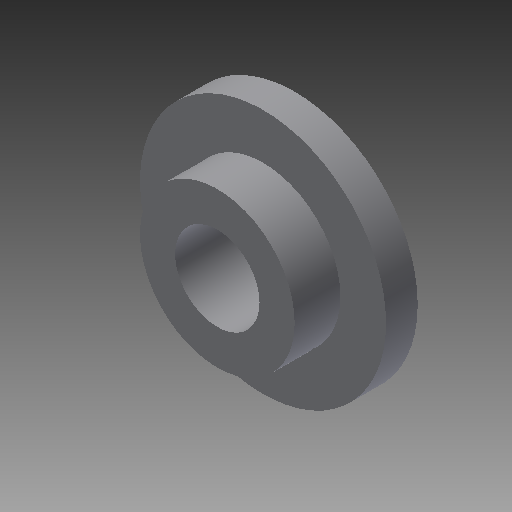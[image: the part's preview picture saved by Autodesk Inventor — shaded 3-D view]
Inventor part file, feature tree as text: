
AUTODESK INVENTOR PART (.ipt)
format: ipt  version: 2017 SP1 (Build 210196100, 196)  size: 103,936 bytes
history: native  units: mm
features: extrude x3, sketch x3
ambient origin geometry x8: Origin, YZ Plane, XZ Plane, XY Plane, X Axis, Y Axis, Z Axis, Center Point
bodies: Solid1 (feature_tree)
feature tree (6):
  extrude  "Extrusion1"  Depth=4.5mm TaperAngle=0.0deg
  extrude  "Extrusion2"  Depth=6.5mm TaperAngle=0.0deg
  extrude  "Extrusion3"  Depth=6.5mm TaperAngle=0.0deg
  sketch  "Sketch1"  dims[d0=35.0mm d1=4.5mm d2=0.0mm]
  sketch  "Sketch2"  dims[d3=22.0mm d4=6.5mm d5=0.0mm]
  sketch  "Sketch3"  dims[d6=12.0mm d7=6.5mm d8=0.0mm]
